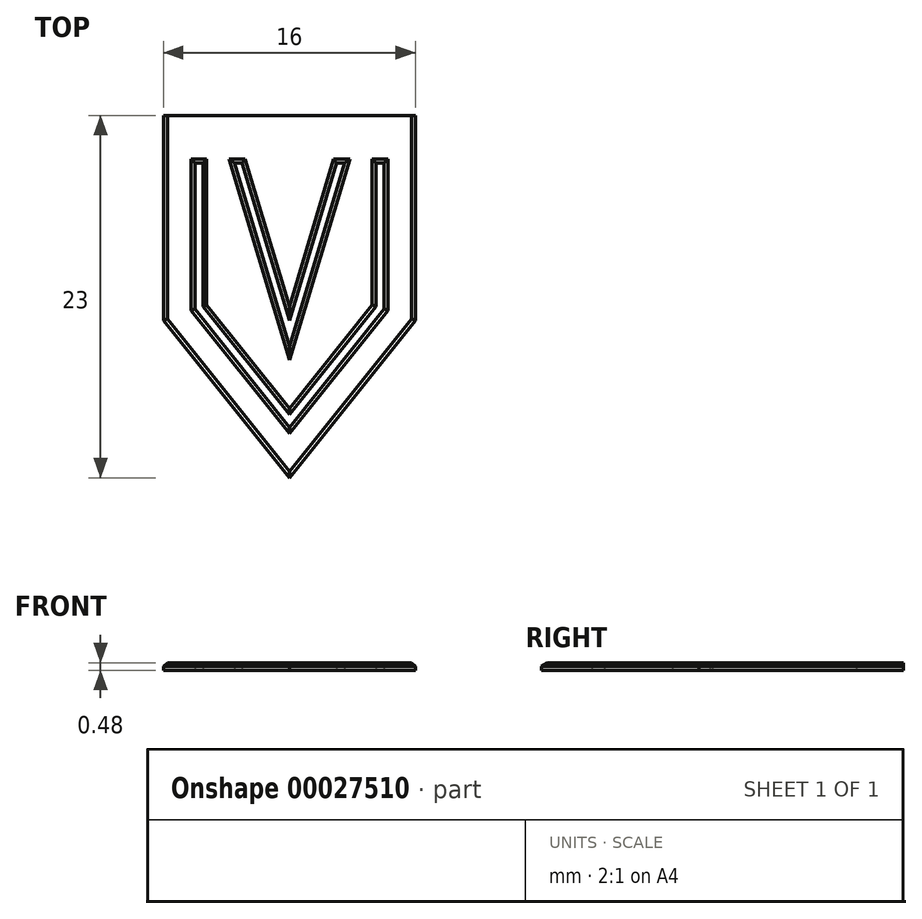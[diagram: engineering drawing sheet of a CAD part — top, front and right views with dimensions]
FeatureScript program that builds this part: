
annotation { "Feature Type Name" : "Feature", "Feature Type Description" : "" }
export const myFeature = defineFeature(function(context is Context, id is Id, definition is map)
    precondition{}
    {
        {
            var Q0;
            Q0=qCreatedBy(makeId("Top.planeOp"),FACE);
            var sketch = newSketch(context, id + "F0", { "sketchPlane" : qUnion([Q0])});
            skLineSegment(sketch, "E0.rect.top", {"start": v(8, 6.5) * mm, "end": v(-8, 6.5) * mm});
            skLineSegment(sketch, "E0.rect.left", {"start": v(8, -6.5) * mm, "end": v(8, 6.5) * mm});
            skLineSegment(sketch, "E0.rect.right", {"start": v(-8, -6.5) * mm, "end": v(-8, 6.5) * mm});
            skLineSegment(sketch, "E1", {"start": v(8, -6.5) * mm, "end": v(0, -16.5) * mm});
            skLineSegment(sketch, "E2", {"start": v(0, -16.5) * mm, "end": v(-8, -6.5) * mm});
            skLineSegment(sketch, "E3.0", {"start": v(6, -5.8) * mm, "end": v(6, 3.5) * mm});
            skLineSegment(sketch, "E3.1", {"start": v(6, -5.8) * mm, "end": v(0, -13.3) * mm});
            skLineSegment(sketch, "E3.2", {"start": v(0, -13.3) * mm, "end": v(-6, -5.8) * mm});
            skLineSegment(sketch, "E3.3", {"start": v(-6, -5.8) * mm, "end": v(-6, 3.5) * mm});
            skLineSegment(sketch, "E4.0", {"start": v(5.5, -5.62) * mm, "end": v(5.5, 3.5) * mm});
            skLineSegment(sketch, "E4.1", {"start": v(5.5, -5.62) * mm, "end": v(0, -12.5) * mm});
            skLineSegment(sketch, "E4.2", {"start": v(0, -12.5) * mm, "end": v(-5.5, -5.62) * mm});
            skLineSegment(sketch, "E4.3", {"start": v(-5.5, -5.62) * mm, "end": v(-5.5, 3.5) * mm});
            skLineSegment(sketch, "E5", {"start": v(6, 3.5) * mm, "end": v(5.5, 3.5) * mm});
            skPoint(sketch, "E6.orphan", {"position": v(8, 3.5) * mm});
            skLineSegment(sketch, "E7.trimOffspring", {"start": v(-5.5, 3.5) * mm, "end": v(-6, 3.5) * mm});
            skLineSegment(sketch, "E8", {"start": v(3, 3.5) * mm, "end": v(0, -6.5) * mm});
            skLineSegment(sketch, "E9", {"start": v(0, 6.5) * mm, "end": v(0, -16.5) * mm});
            skPoint(sketch, "E10.MirrorCS.end.orphan", {"position": v(0, -6.5) * mm});
            skLineSegment(sketch, "E11.MirrorCS", {"start": v(-3, 3.5) * mm, "end": v(0, -6.5) * mm});
            skLineSegment(sketch, "E12", {"start": v(3.5, 3.5) * mm, "end": v(0, -8.17) * mm});
            skLineSegment(sketch, "E13.MirrorCS", {"start": v(-3.5, 3.5) * mm, "end": v(0, -8.17) * mm});
            skLineSegment(sketch, "E14", {"start": v(3.5, 3.5) * mm, "end": v(3, 3.5) * mm});
            skLineSegment(sketch, "E15", {"start": v(-3, 3.5) * mm, "end": v(-3.5, 3.5) * mm});
            skSolve(sketch);
        }
        {
            var Q0;
            Q0 = qSketchRegion(id + "F0", true);
            extrude(context, id + "F1", {"entities" : qUnion([Q0]), "offsetDistance" : 25 * mm, "depth" : 0.48 * mm});
        }
        {
            var Q0;
            Q0=makeQuery(id+"F1.opExtrude","CAP_EDGE",EDGE,{"disambiguationData":[OSD([sQuery(id+"F0.wireOp",EDGE,"E2")])],"isStart":false});
            var Q1;
            Q1=makeQuery(id+"F1.opExtrude","CAP_EDGE",EDGE,{"disambiguationData":[OSD([sQuery(id+"F0.wireOp",EDGE,"E0.rect.right")])],"isStart":false});
            var Q2;
            Q2=makeQuery(id+"F1.opExtrude","CAP_EDGE",EDGE,{"disambiguationData":[OSD([sQuery(id+"F0.wireOp",EDGE,"E1")])],"isStart":false});
            var Q3;
            Q3=makeQuery(id+"F1.opExtrude","CAP_EDGE",EDGE,{"disambiguationData":[OSD([sQuery(id+"F0.wireOp",EDGE,"E0.rect.left")])],"isStart":false});
            var Q4;
            Q4=makeQuery(id+"F1.opExtrude","CAP_EDGE",EDGE,{"disambiguationData":[OSD([sQuery(id+"F0.wireOp",EDGE,"E3.0")])],"isStart":false});
            var Q5;
            Q5=makeQuery(id+"F1.opExtrude","CAP_EDGE",EDGE,{"disambiguationData":[OSD([sQuery(id+"F0.wireOp",EDGE,"E3.1")])],"isStart":false});
            var Q6;
            Q6=makeQuery(id+"F1.opExtrude","CAP_EDGE",EDGE,{"disambiguationData":[OSD([sQuery(id+"F0.wireOp",EDGE,"E3.2")])],"isStart":false});
            var Q7;
            Q7=makeQuery(id+"F1.opExtrude","CAP_EDGE",EDGE,{"disambiguationData":[OSD([sQuery(id+"F0.wireOp",EDGE,"E3.3")])],"isStart":false});
            var Q8;
            Q8=makeQuery(id+"F1.opExtrude","CAP_EDGE",EDGE,{"disambiguationData":[OSD([sQuery(id+"F0.wireOp",EDGE,"E4.3")])],"isStart":false});
            var Q9;
            Q9=makeQuery(id+"F1.opExtrude","CAP_EDGE",EDGE,{"disambiguationData":[OSD([sQuery(id+"F0.wireOp",EDGE,"E4.2")])],"isStart":false});
            var Q10;
            Q10=makeQuery(id+"F1.opExtrude","CAP_EDGE",EDGE,{"disambiguationData":[OSD([sQuery(id+"F0.wireOp",EDGE,"E4.1")])],"isStart":false});
            var Q11;
            Q11=makeQuery(id+"F1.opExtrude","CAP_EDGE",EDGE,{"disambiguationData":[OSD([sQuery(id+"F0.wireOp",EDGE,"E4.0")])],"isStart":false});
            var Q12;
            Q12=makeQuery(id+"F1.opExtrude","CAP_EDGE",EDGE,{"disambiguationData":[OSD([sQuery(id+"F0.wireOp",EDGE,"64e674a0-e40b-498e-bb16-1642b327c830.0")])],"isStart":false});
            var Q13;
            Q13=makeQuery(id+"F1.opExtrude","CAP_EDGE",EDGE,{"disambiguationData":[OSD([sQuery(id+"F0.wireOp",EDGE,"b6481ea3-303d-4717-a5c3-7fb8478ac7ba.0")])],"isStart":false});
            var Q14;
            Q14=makeQuery(id+"F1.opExtrude","CAP_EDGE",EDGE,{"disambiguationData":[OSD([sQuery(id+"F0.wireOp",EDGE,"b6481ea3-303d-4717-a5c3-7fb8478ac7ba.1")])],"isStart":false});
            var Q15;
            Q15=makeQuery(id+"F1.opExtrude","CAP_EDGE",EDGE,{"disambiguationData":[OSD([sQuery(id+"F0.wireOp",EDGE,"b6481ea3-303d-4717-a5c3-7fb8478ac7ba.2")])],"isStart":false});
            var Q16;
            Q16=makeQuery(id+"F1.opExtrude","CAP_EDGE",EDGE,{"disambiguationData":[OSD([sQuery(id+"F0.wireOp",EDGE,"b6481ea3-303d-4717-a5c3-7fb8478ac7ba.3")])],"isStart":false});
            var Q17;
            Q17=makeQuery(id+"F1.opExtrude","CAP_EDGE",EDGE,{"disambiguationData":[OSD([sQuery(id+"F0.wireOp",EDGE,"64e674a0-e40b-498e-bb16-1642b327c830.2")])],"isStart":false});
            var Q18;
            Q18=makeQuery(id+"F1.opExtrude","CAP_EDGE",EDGE,{"disambiguationData":[OSD([sQuery(id+"F0.wireOp",EDGE,"64e674a0-e40b-498e-bb16-1642b327c830.1")])],"isStart":false});
            var Q19;
            Q19=makeQuery(id+"F1.opExtrude","CAP_EDGE",EDGE,{"disambiguationData":[OSD([sQuery(id+"F0.wireOp",EDGE,"64e674a0-e40b-498e-bb16-1642b327c830.3")])],"isStart":false});
            var Q20;
            Q20=makeQuery(id+"F1.opExtrude","CAP_EDGE",EDGE,{"disambiguationData":[OSD([sQuery(id+"F0.wireOp",EDGE,"E11.MirrorCS")])],"isStart":false});
            var Q21;
            Q21=makeQuery(id+"F1.opExtrude","CAP_EDGE",EDGE,{"disambiguationData":[OSD([sQuery(id+"F0.wireOp",EDGE,"E13.MirrorCS")])],"isStart":false});
            var Q22;
            Q22=makeQuery(id+"F1.opExtrude","CAP_EDGE",EDGE,{"disambiguationData":[OSD([sQuery(id+"F0.wireOp",EDGE,"E8")])],"isStart":false});
            var Q23;
            Q23=makeQuery(id+"F1.opExtrude","CAP_EDGE",EDGE,{"disambiguationData":[OSD([sQuery(id+"F0.wireOp",EDGE,"E15")])],"isStart":false});
            var Q24;
            Q24=makeQuery(id+"F1.opExtrude","CAP_EDGE",EDGE,{"disambiguationData":[OSD([sQuery(id+"F0.wireOp",EDGE,"E14")])],"isStart":false});
            var Q25;
            Q25=makeQuery(id+"F1.opExtrude","CAP_EDGE",EDGE,{"disambiguationData":[OSD([sQuery(id+"F0.wireOp",EDGE,"E12")])],"isStart":false});
            var Q26;
            Q26=makeQuery(id+"F1.opExtrude","CAP_EDGE",EDGE,{"disambiguationData":[OSD([sQuery(id+"F0.wireOp",EDGE,"E7.trimOffspring")])],"isStart":false});
            var Q27;
            Q27=makeQuery(id+"F1.opExtrude","CAP_EDGE",EDGE,{"disambiguationData":[OSD([sQuery(id+"F0.wireOp",EDGE,"E5")])],"isStart":false});
            chamfer(context, id + "F2", {"entities" : qUnion([Q0, Q1, Q2, Q3, Q4, Q5, Q6, Q7, Q8, Q9, Q10, Q11, Q12, Q13, Q14, Q15, Q16, Q17, Q18, Q19, Q20, Q21, Q22, Q23, Q24, Q25, Q26, Q27]), "width" : 0.25 * mm, "tangentPropagation" : true});
        }
    });
